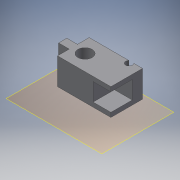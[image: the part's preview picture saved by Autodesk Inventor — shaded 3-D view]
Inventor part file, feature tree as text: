
AUTODESK INVENTOR PART (.ipt)
format: ipt  version: 2017 (Build 210142000, 142)  size: 133,120 bytes
history: native  units: mm
features: extrude x3, sketch x3, other x3, reference x2, plane x1, projected_geometry x1
ambient origin geometry x8: Origin, YZ Plane, XZ Plane, XY Plane, X Axis, Y Axis, Z Axis, Center Point
bodies: Solid1 (feature_tree)
feature tree (13):
  plane  "Work Plane1"
  extrude  "Extrusion1"  Depth=0.2mm
  extrude  "Extrusion2"  Depth=0.2mm
  extrude  "Extrusion3"  Depth=15.0mm TaperAngle=0.0deg
  sketch  "Sketch1"  dims[d0=0.2mm d1=0.2mm]
  reference  "Reference1"
  sketch  "Sketch2"  dims[d2=0.2mm d3=0.2mm]
  reference  "Reference2"
  sketch  "Sketch3"  dims[d4=30.0mm d5=15.0mm d6=0.0mm d7=15.0mm d8=0.0mm d9=10.0mm d10=12.0mm d11=10.0mm d12=0.0mm]
  projected_geometry  "Projected Loop1"
  parser-record x1  (decoder bookkeeping rows leaked as tree rows — omitted from the tree; the rows remain in map.json)
  other  "gearbox.iam"
  other  "shifter box 1:1"
note: 1 file-system path scrubbed to <path> (originals preserved in map.json)
